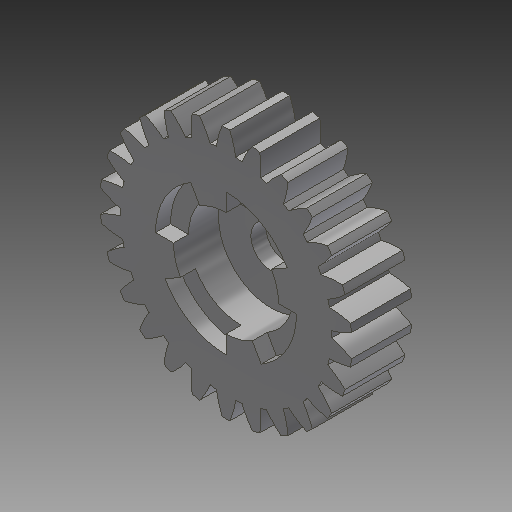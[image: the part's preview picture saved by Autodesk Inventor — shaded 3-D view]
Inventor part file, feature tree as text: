
AUTODESK INVENTOR PART (.ipt)
format: ipt  version: 2017 (Build 210142000, 142)  size: 297,984 bytes
history: native  units: mm (DEFAULTED — no unit token found)
features: sketch x5, extrude x4, plane x3, other x3, pattern_circular x1
ambient origin geometry x8: Origin, YZ Plane, XZ Plane, XY Plane, X Axis, Y Axis, Z Axis, Center Point
bodies: Solid1 (feature_tree)
feature tree (16):
  extrude  "Extrusion1"  Depth=20.0mm TaperAngle=0.0deg
  plane  "Work Plane2"
  plane  "Work Plane8"
  plane  "Work Plane9"
  other  "Spur Gear"
  extrude  "Extrusion2"  Depth=10.0mm TaperAngle=0.0deg
  extrude  "Extrusion3"  Depth=1.208305mm TaperAngle=0.0deg
  extrude  "Extrusion4"  TaperAngle=0.0deg  [1 undecoded]
  pattern_circular  "Circular Pattern1"  Count=8  [1 undecoded]
  sketch  "Sketch1"  dims[d0=83.976768mm d1=20.0mm d2=0.0mm]
  sketch  "Sketch2"  dims[d3=78.490566mm d4=10.0mm d5=0.0mm]
  other  "Srf1"
  sketch  "Sketch3"  dims[d16=80.0mm d17=0.0mm d34=1.208305mm]
  sketch  "Sketch4"  dims[d39=0.0mm d41=0.0mm d43=80.0mm]
  sketch  "Sketch5"  dims[d46=80.0mm d47=0.0mm d48=0.0mm d49=13.5mm d50=10.0mm d51=0.0mm d52=35.0mm d53=15.0mm d54=0.0mm d55=6.0mm d56=60.0deg d57=5.0mm d58=0.0mm d59=40.0mm d60=360.0deg]
  other  "Pitch Diameter"
note: 2 required parameter values undecoded (feature->parameter linkage not recoverable at this tier; creation-order binding heuristic only, values carry confidence <= 0.55)
